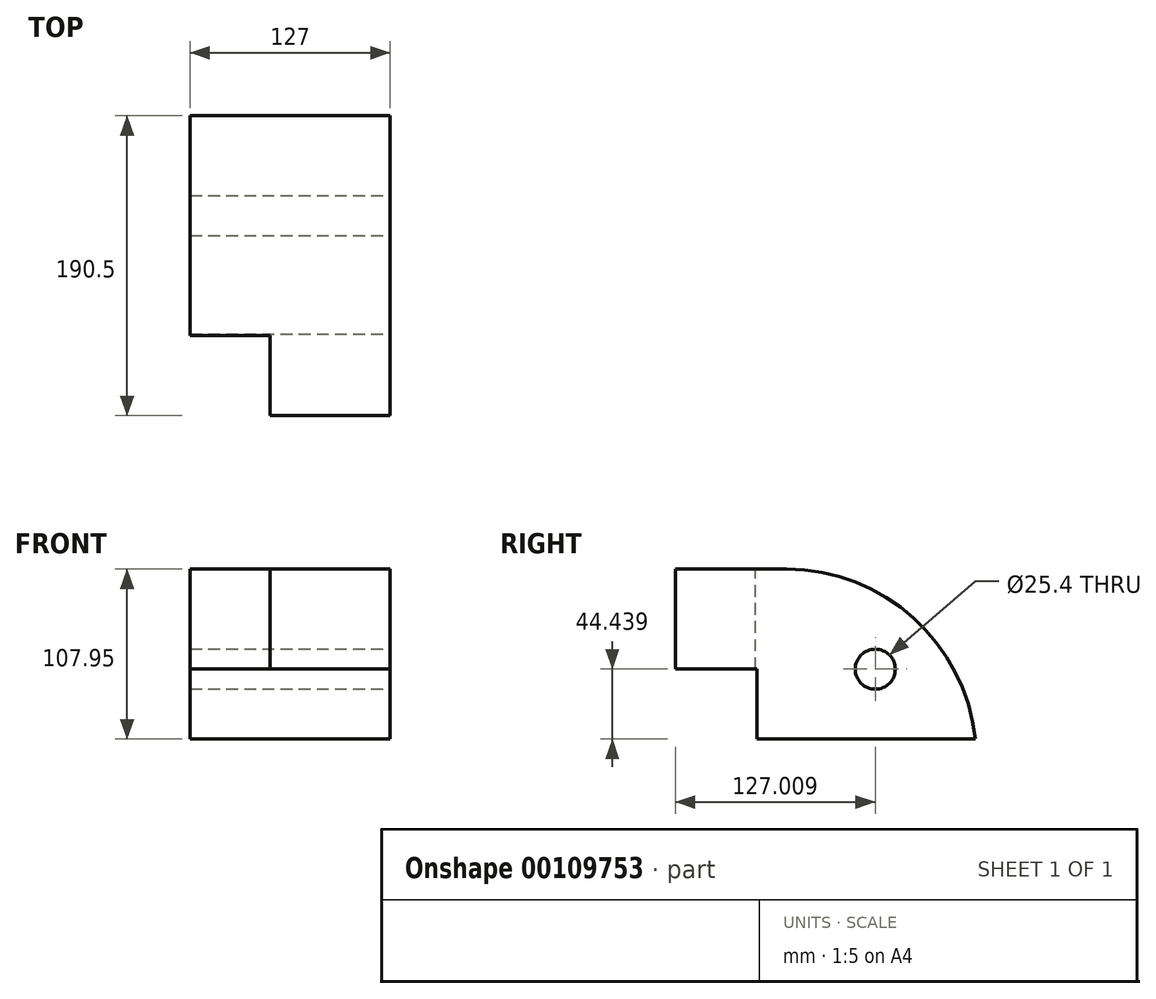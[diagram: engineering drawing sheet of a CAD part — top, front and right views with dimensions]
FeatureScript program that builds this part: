
annotation { "Feature Type Name" : "Feature", "Feature Type Description" : "" }
export const myFeature = defineFeature(function(context is Context, id is Id, definition is map)
    precondition{}
    {
        {
            var Q0;
            Q0=qCreatedBy(makeId("Front.planeOp"),FACE);
            var sketch = newSketch(context, id + "F0", { "sketchPlane" : qUnion([Q0])});
            skLineSegment(sketch, "E0.bottom", {"start": v(-37.32, 0) * mm, "end": v(89.68, 0) * mm});
            skLineSegment(sketch, "E0.top", {"start": v(-37.32, 107.95) * mm, "end": v(89.68, 107.95) * mm});
            skLineSegment(sketch, "E0.left", {"start": v(-37.32, 0) * mm, "end": v(-37.32, 107.95) * mm});
            skLineSegment(sketch, "E0.right", {"start": v(89.68, 0) * mm, "end": v(89.68, 107.95) * mm});
            skSolve(sketch);
        }
        {
            var Q0;
            Q0=makeQuery(id+"F0.imprint","IMPRINT",FACE,{"disambiguationData":[TD([[makeQuery(id+"F0.imprint","IMPRINT",EDGE,{"derivedFrom":sQuery(id+"F0.wireOp",EDGE,"E0.bottom")}),1.0]])]});
            extrude(context, id + "F1", {"entities" : qUnion([Q0]), "depth" : 139.7 * mm});
        }
        {
            var Q0;
            Q0=makeQuery(id+"F1.opExtrude","CAP_FACE",FACE,{"disambiguationData":[OSD([sQuery(id+"F0.wireOp",EDGE,"E0.bottom"),sQuery(id+"F0.wireOp",EDGE,"E0.top"),sQuery(id+"F0.wireOp",EDGE,"E0.left"),sQuery(id+"F0.wireOp",EDGE,"E0.right")])],"isStart":false});
            var sketch = newSketch(context, id + "F2", { "sketchPlane" : qUnion([Q0])});
            skLineSegment(sketch, "E1.bottom", {"start": v(89.68, 107.95) * mm, "end": v(13.48, 107.95) * mm});
            skLineSegment(sketch, "E1.top", {"start": v(89.68, 44.45) * mm, "end": v(13.48, 44.45) * mm});
            skLineSegment(sketch, "E1.left", {"start": v(89.68, 107.95) * mm, "end": v(89.68, 44.45) * mm});
            skLineSegment(sketch, "E1.right", {"start": v(13.48, 107.95) * mm, "end": v(13.48, 44.45) * mm});
            skSolve(sketch);
        }
        {
            var Q0;
            Q0=makeQuery(id+"F2.imprint","IMPRINT",FACE,{"disambiguationData":[TD([[makeQuery(id+"F2.imprint","IMPRINT",EDGE,{"derivedFrom":sQuery(id+"F2.wireOp",EDGE,"E1.bottom")}),-1.0]])]});
            extrude(context, id + "F3", {"entities" : qUnion([Q0]), "operationType" : NewBodyOperationType.ADD, "depth" : 50.8 * mm});
        }
        {
            var Q0;
            Q0=makeQuery(id+"F1.opExtrude","CAP_FACE",FACE,{"disambiguationData":[OSD([sQuery(id+"F0.wireOp",EDGE,"E0.bottom"),sQuery(id+"F0.wireOp",EDGE,"E0.top"),sQuery(id+"F0.wireOp",EDGE,"E0.left"),sQuery(id+"F0.wireOp",EDGE,"E0.right")])],"isStart":false});
            var sketch = newSketch(context, id + "F4", { "sketchPlane" : qUnion([Q0])});
            skLineSegment(sketch, "E2.bottom", {"start": v(89.68, 44.45) * mm, "end": v(-37.32, 44.45) * mm});
            skLineSegment(sketch, "E2.top", {"start": v(89.68, 0) * mm, "end": v(-37.32, 0) * mm});
            skLineSegment(sketch, "E2.left", {"start": v(89.68, 44.45) * mm, "end": v(89.68, 0) * mm});
            skLineSegment(sketch, "E2.right", {"start": v(-37.32, 44.45) * mm, "end": v(-37.32, 0) * mm});
            skSolve(sketch);
        }
        {
            var Q0;
            Q0=makeQuery(id+"F4.imprint","IMPRINT",FACE,{"disambiguationData":[TD([[makeQuery(id+"F4.imprint","IMPRINT",EDGE,{"derivedFrom":sQuery(id+"F4.wireOp",EDGE,"E2.top")}),1.0]])]});
            extrude(context, id + "F5", {"entities" : qUnion([Q0]), "operationType" : NewBodyOperationType.REMOVE, "oppositeDirection" : true, "depth" : mm});
        }
        {
            var Q0;
            Q0=makeQuery(id+"F1.opExtrude","CAP_EDGE",EDGE,{"disambiguationData":[OSD([sQuery(id+"F0.wireOp",EDGE,"E0.top")])],"isStart":true});
            fillet(context, id + "F6", {"entities" : qUnion([Q0]), "radius" : 120.65 * mm, "tangentPropagation" : true, "allowEdgeOverflow" : false});
        }
        {
            var Q0;
            Q0=makeQuery(id+"F3.boolean.opBoolean","MERGE",FACE,{"derivedFrom":[makeQuery(id+"F1.opExtrude","SWEPT_FACE",FACE,{"disambiguationData":[OSD([sQuery(id+"F0.wireOp",EDGE,"E0.right")])]}),makeQuery(id+"F3.opExtrude","SWEPT_FACE",FACE,{"disambiguationData":[OSD([sQuery(id+"F2.wireOp",EDGE,"E1.left")])]})]});
            var sketch = newSketch(context, id + "F7", { "sketchPlane" : qUnion([Q0])});
            skLineSegment(sketch, "E3", {"start": v(0, 0) * mm, "end": v(-63.5, 0) * mm});
            skLineSegment(sketch, "E4", {"start": v(-63.5, 0) * mm, "end": v(-63.5, 44.44) * mm});
            skCircle(sketch, "E5", {"center": v(-63.5, 44.44) * mm, "radius": 12.7 * mm});
            skSolve(sketch);
        }
        {
            var Q0;
            Q0=makeQuery(id+"F7.imprint","IMPRINT",FACE,{"disambiguationData":[TD([[makeQuery(id+"F7.imprint","IMPRINT",EDGE,{"derivedFrom":sQuery(id+"F7.wireOp",EDGE,"E5")}),1.0]])]});
            extrude(context, id + "F8", {"entities" : qUnion([Q0]), "operationType" : NewBodyOperationType.REMOVE, "oppositeDirection" : true, "depth" : 143 * mm});
        }
    });
